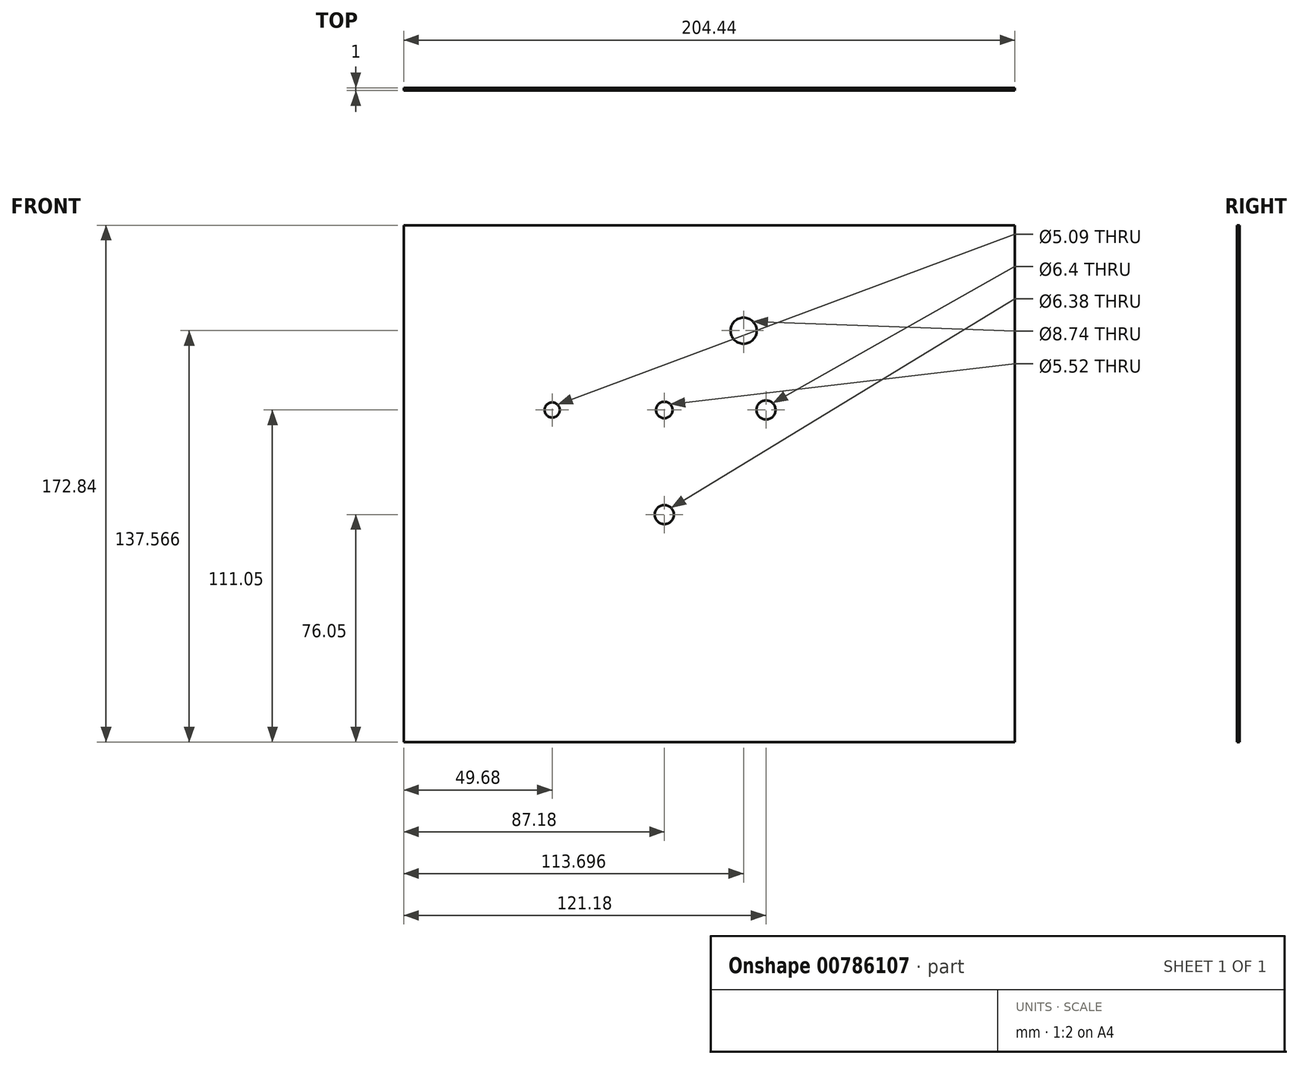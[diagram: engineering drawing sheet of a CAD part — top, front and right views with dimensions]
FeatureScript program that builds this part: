
annotation { "Feature Type Name" : "Feature", "Feature Type Description" : "" }
export const myFeature = defineFeature(function(context is Context, id is Id, definition is map)
    precondition{}
    {
        {
            var Q0;
            Q0=qCreatedBy(makeId("Front.planeOp"),FACE);
            var sketch = newSketch(context, id + "F0", { "sketchPlane" : qUnion([Q0])});
            skLineSegment(sketch, "E0.bottom", {"start": v(-49.68, 61.8) * mm, "end": v(154.76, 61.8) * mm});
            skLineSegment(sketch, "E0.top", {"start": v(-49.68, -111.05) * mm, "end": v(154.76, -111.05) * mm});
            skLineSegment(sketch, "E0.left", {"start": v(-49.68, 61.8) * mm, "end": v(-49.68, -111.05) * mm});
            skLineSegment(sketch, "E0.right", {"start": v(154.76, 61.8) * mm, "end": v(154.76, -111.05) * mm});
            skCircle(sketch, "E1", {"center": v(0, 0) * mm, "radius": 2.55 * mm});
            skCircle(sketch, "E2", {"center": v(37.5, 0) * mm, "radius": 2.76 * mm});
            skCircle(sketch, "E3", {"center": v(71.5, 0) * mm, "radius": 3.2 * mm});
            skCircle(sketch, "E4", {"center": v(37.5, -35) * mm, "radius": 3.19 * mm});
            skCircle(sketch, "E5", {"center": v(64.02, 26.52) * mm, "radius": 4.37 * mm});
            skLineSegment(sketch, "E6", {"start": v(64.02, 26.52) * mm, "end": v(37.5, 0) * mm});
            skSolve(sketch);
        }
        {
            var Q0;
            Q0=makeQuery(id+"F0.imprint","IMPRINT",FACE,{"disambiguationData":[TD([[makeQuery(id+"F0.imprint","IMPRINT",EDGE,{"derivedFrom":sQuery(id+"F0.wireOp",EDGE,"E0.bottom")}),-1.0]])]});
            extrude(context, id + "F1", {"entities" : qUnion([Q0]), "depth" : 1 * mm, "offsetDistance" : 25 * mm});
        }
    });
